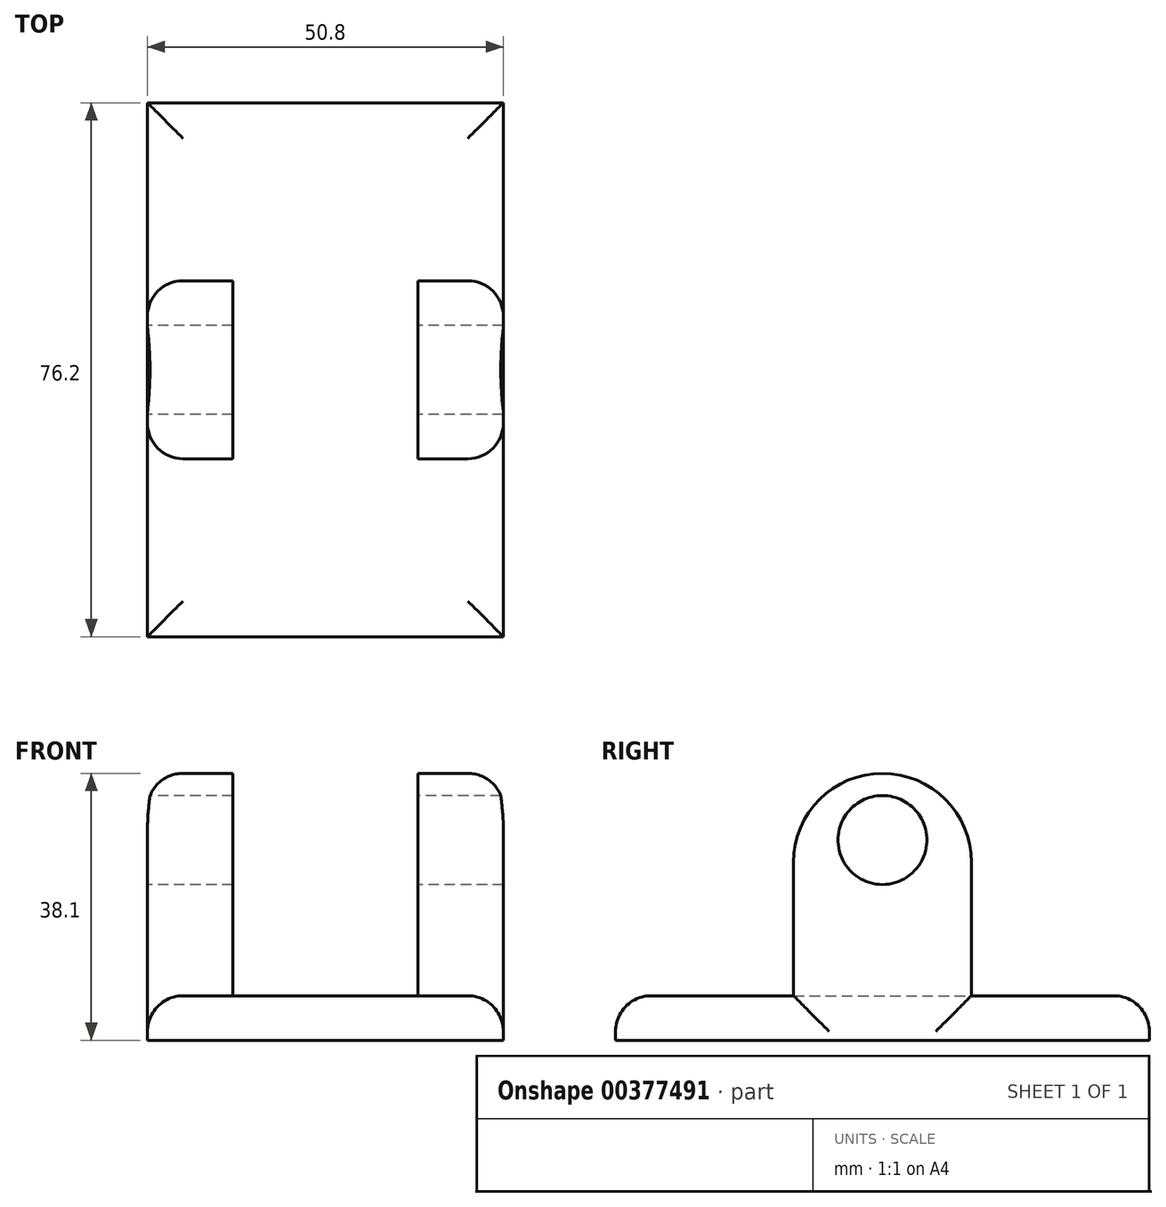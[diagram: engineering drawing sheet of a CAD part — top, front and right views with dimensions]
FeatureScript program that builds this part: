
annotation { "Feature Type Name" : "Feature", "Feature Type Description" : "" }
export const myFeature = defineFeature(function(context is Context, id is Id, definition is map)
    precondition{}
    {
        {
            var Q0;
            Q0=qCreatedBy(makeId("Top.planeOp"),FACE);
            var sketch = newSketch(context, id + "F0", { "sketchPlane" : qUnion([Q0])});
            skLineSegment(sketch, "E0.bottom", {"start": v(25.4, -38.1) * mm, "end": v(-25.4, -38.1) * mm});
            skLineSegment(sketch, "E0.top", {"start": v(25.4, 38.1) * mm, "end": v(-25.4, 38.1) * mm});
            skLineSegment(sketch, "E0.left", {"start": v(25.4, -38.1) * mm, "end": v(25.4, 38.1) * mm});
            skLineSegment(sketch, "E0.right", {"start": v(-25.4, -38.1) * mm, "end": v(-25.4, 38.1) * mm});
            skPoint(sketch, "E0.middle", {"position": v(0, 0) * mm});
            skSolve(sketch);
        }
        {
            var Q0;
            Q0 = qSketchRegion(id + "F0", true);
            extrude(context, id + "F1", {"entities" : qUnion([Q0]), "depth" : 6.35 * mm});
        }
        {
            var Q0;
            Q0=makeQuery(id+"F1.opExtrude","CAP_FACE",FACE,{"disambiguationData":[OSD([sQuery(id+"F0.wireOp",EDGE,"E0.bottom"),sQuery(id+"F0.wireOp",EDGE,"E0.top"),sQuery(id+"F0.wireOp",EDGE,"E0.left"),sQuery(id+"F0.wireOp",EDGE,"E0.right")])],"isStart":false});
            var sketch = newSketch(context, id + "F2", { "sketchPlane" : qUnion([Q0])});
            skLineSegment(sketch, "E1.bottom", {"start": v(-13.2, -12.7) * mm, "end": v(-25.4, -12.7) * mm});
            skLineSegment(sketch, "E1.top", {"start": v(-13.2, 12.7) * mm, "end": v(-25.4, 12.7) * mm});
            skLineSegment(sketch, "E1.left", {"start": v(-13.2, -12.7) * mm, "end": v(-13.2, 12.7) * mm});
            skLineSegment(sketch, "E1.right", {"start": v(-25.4, -12.7) * mm, "end": v(-25.4, 12.7) * mm});
            skPoint(sketch, "E1.middle", {"position": v(-19.3, 0) * mm});
            skLineSegment(sketch, "E2.MirrorCS", {"start": v(13.2, 12.7) * mm, "end": v(25.4, 12.7) * mm});
            skLineSegment(sketch, "E3.MirrorCS", {"start": v(13.2, -12.7) * mm, "end": v(13.2, 12.7) * mm});
            skLineSegment(sketch, "E4.MirrorCS", {"start": v(13.2, -12.7) * mm, "end": v(25.4, -12.7) * mm});
            skLineSegment(sketch, "E5.MirrorCS", {"start": v(25.4, -12.7) * mm, "end": v(25.4, 12.7) * mm});
            skSolve(sketch);
        }
        {
            var Q0;
            Q0 = qSketchRegion(id + "F2", true);
            extrude(context, id + "F3", {"entities" : qUnion([Q0]), "operationType" : NewBodyOperationType.ADD, "depth" : 31.75 * mm});
        }
        {
            var Q0;
            Q0=makeQuery(id+"F3.boolean.opBoolean","MERGE",FACE,{"derivedFrom":[makeQuery(id+"F1.opExtrude","SWEPT_FACE",FACE,{"disambiguationData":[OSD([sQuery(id+"F0.wireOp",EDGE,"E0.right")])]}),makeQuery(id+"F3.opExtrude","SWEPT_FACE",FACE,{"disambiguationData":[OSD([sQuery(id+"F2.wireOp",EDGE,"E1.right")])]})]});
            var sketch = newSketch(context, id + "F4", { "sketchPlane" : qUnion([Q0])});
            skLineSegment(sketch, "E6", {"start": v(0, 38.1) * mm, "end": v(0, 0) * mm});
            skLineSegment(sketch, "E7", {"start": v(0, 0) * mm, "end": v(0, 19.05) * mm});
            skLineSegment(sketch, "E8", {"start": v(0, 19.05) * mm, "end": v(0, 38.1) * mm});
            skLineSegment(sketch, "E9", {"start": v(0, 38.1) * mm, "end": v(0, 28.58) * mm});
            skSolve(sketch);
        }
        {
            var Q0;
            Q0=sQuery(id+"F4.wireOp",VERTEX,"E9.end");
            var Q1;
            Q1=makeQuery(id+"F1.opExtrude","SWEPT_BODY",BODY,{"disambiguationData":[OSD([sQuery(id+"F0.wireOp",EDGE,"E0.bottom"),sQuery(id+"F0.wireOp",EDGE,"E0.top"),sQuery(id+"F0.wireOp",EDGE,"E0.left"),sQuery(id+"F0.wireOp",EDGE,"E0.right")])]});
            hole(context, id + "F5", {"style" : HoleStyle.SIMPLE, "endStyle" : HoleEndStyle.BLIND, "holeDiameter" : 12.7 * mm, "holeDepth" : 254 * mm, "tappedDepth" : 12.7 * mm, "tapClearance" : 3, "locations" : qUnion([Q0]), "scope" : qUnion([Q1])});
        }
        {
            var Q0;
            Q0=makeQuery(id+"F3.opExtrude","CAP_EDGE",EDGE,{"disambiguationData":[OSD([sQuery(id+"F2.wireOp",EDGE,"E2.MirrorCS")])],"isStart":false});
            var Q1;
            Q1=makeQuery(id+"F3.opExtrude","CAP_EDGE",EDGE,{"disambiguationData":[OSD([sQuery(id+"F2.wireOp",EDGE,"E4.MirrorCS")])],"isStart":false});
            var Q2;
            Q2=makeQuery(id+"F3.opExtrude","CAP_EDGE",EDGE,{"disambiguationData":[OSD([sQuery(id+"F2.wireOp",EDGE,"E1.top")])],"isStart":false});
            var Q3;
            Q3=makeQuery(id+"F3.opExtrude","CAP_EDGE",EDGE,{"disambiguationData":[OSD([sQuery(id+"F2.wireOp",EDGE,"E1.bottom")])],"isStart":false});
            fillet(context, id + "F6", {"entities" : qUnion([Q0, Q1, Q2, Q3]), "radius" : 12.7 * mm, "tangentPropagation" : true, "allowEdgeOverflow" : false});
        }
        {
            var Q0;
            Q0=makeQuery(id+"F3.opExtrude","SWEPT_EDGE",EDGE,{"disambiguationData":[OSD([sQuery(id+"F0.wireOp",EDGE,"E0.right"),sQuery(id+"F2.wireOp",EDGE,"E1.top"),sQuery(id+"F2.wireOp",EDGE,"E1.right")])]});
            var Q1;
            Q1=makeQuery(id+"F3.opExtrude","SWEPT_EDGE",EDGE,{"disambiguationData":[OSD([sQuery(id+"F0.wireOp",EDGE,"E0.left"),sQuery(id+"F2.wireOp",EDGE,"E4.MirrorCS"),sQuery(id+"F2.wireOp",EDGE,"E5.MirrorCS")])]});
            var Q2;
            Q2=makeQuery(id+"F1.opExtrude","CAP_EDGE",EDGE,{"disambiguationData":[OSD([sQuery(id+"F0.wireOp",EDGE,"E0.bottom")])],"isStart":false});
            var Q3;
            {var subQ0=sQuery(id+"F0.wireOp",EDGE,"E0.bottom");var subQ1=sQuery(id+"F0.wireOp",EDGE,"E0.left");Q3=makeQuery(id+"F3.boolean.opBoolean","SPLIT",EDGE,{"disambiguationData":[TD([makeQuery(id+"F1.opExtrude","SWEPT_FACE",FACE,{"disambiguationData":[OSD([subQ0])]})])],"derivedFrom":makeQuery(id+"F1.opExtrude","CAP_EDGE",EDGE,{"disambiguationData":[OSD([subQ1])],"isStart":false})});}
            var Q4;
            {var subQ0=sQuery(id+"F0.wireOp",EDGE,"E0.left");var subQ1=sQuery(id+"F0.wireOp",EDGE,"E0.top");Q4=makeQuery(id+"F3.boolean.opBoolean","SPLIT",EDGE,{"disambiguationData":[TD([makeQuery(id+"F1.opExtrude","SWEPT_FACE",FACE,{"disambiguationData":[OSD([subQ1])]})])],"derivedFrom":makeQuery(id+"F1.opExtrude","CAP_EDGE",EDGE,{"disambiguationData":[OSD([subQ0])],"isStart":false})});}
            var Q5;
            {var subQ0=sQuery(id+"F0.wireOp",EDGE,"E0.right");var subQ1=sQuery(id+"F0.wireOp",EDGE,"E0.top");Q5=makeQuery(id+"F3.boolean.opBoolean","SPLIT",EDGE,{"disambiguationData":[TD([makeQuery(id+"F1.opExtrude","SWEPT_FACE",FACE,{"disambiguationData":[OSD([subQ1])]})])],"derivedFrom":makeQuery(id+"F1.opExtrude","CAP_EDGE",EDGE,{"disambiguationData":[OSD([subQ0])],"isStart":false})});}
            var Q6;
            Q6=makeQuery(id+"F1.opExtrude","CAP_EDGE",EDGE,{"disambiguationData":[OSD([sQuery(id+"F0.wireOp",EDGE,"E0.top")])],"isStart":false});
            var Q7;
            {var subQ0=sQuery(id+"F0.wireOp",EDGE,"E0.right");var subQ1=sQuery(id+"F0.wireOp",EDGE,"E0.bottom");Q7=makeQuery(id+"F3.boolean.opBoolean","SPLIT",EDGE,{"disambiguationData":[TD([makeQuery(id+"F1.opExtrude","SWEPT_FACE",FACE,{"disambiguationData":[OSD([subQ1])]})])],"derivedFrom":makeQuery(id+"F1.opExtrude","CAP_EDGE",EDGE,{"disambiguationData":[OSD([subQ0])],"isStart":false})});}
            fillet(context, id + "F7", {"entities" : qUnion([Q0, Q1, Q2, Q3, Q4, Q5, Q6, Q7]), "radius" : 5.08 * mm, "tangentPropagation" : true, "allowEdgeOverflow" : false});
        }
    });
